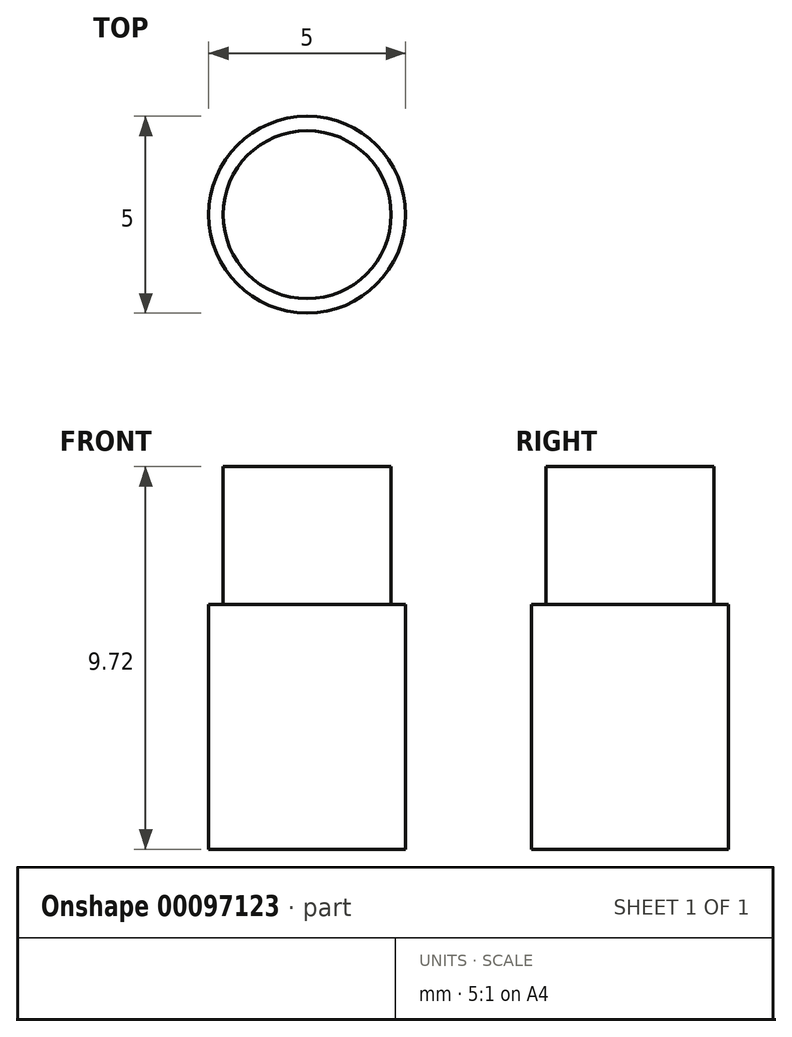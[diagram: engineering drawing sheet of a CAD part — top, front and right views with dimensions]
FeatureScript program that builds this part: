
annotation { "Feature Type Name" : "Feature", "Feature Type Description" : "" }
export const myFeature = defineFeature(function(context is Context, id is Id, definition is map)
    precondition{}
    {
        {
            var Q0;
            Q0=qCreatedBy(makeId("Front.planeOp"),FACE);
            var sketch = newSketch(context, id + "F0", { "sketchPlane" : qUnion([Q0])});
            skLineSegment(sketch, "E0", {"start": v(0, 0) * mm, "end": v(-2.5, 0) * mm});
            skLineSegment(sketch, "E1", {"start": v(-2.5, 0) * mm, "end": v(-2.5, 6.22) * mm});
            skLineSegment(sketch, "E2", {"start": v(-2.5, 6.22) * mm, "end": v(-2.13, 6.22) * mm});
            skLineSegment(sketch, "E3", {"start": v(-2.13, 6.22) * mm, "end": v(-2.13, 9.72) * mm});
            skLineSegment(sketch, "E4", {"start": v(-2.13, 9.72) * mm, "end": v(0, 9.72) * mm});
            skLineSegment(sketch, "E5", {"start": v(0, 9.72) * mm, "end": v(0, 0) * mm});
            skSolve(sketch);
        }
        {
            var Q0;
            Q0=qSketchRegion(id+"F0",true);
            var Q1;
            Q1=sQuery(id+"F0.wireOp",EDGE,"E5");
            revolve(context, id + "F1", {"entities" : qUnion([Q0]), "axis" : qUnion([Q1]), "revolveType" : RevolveType.FULL});
        }
    });
